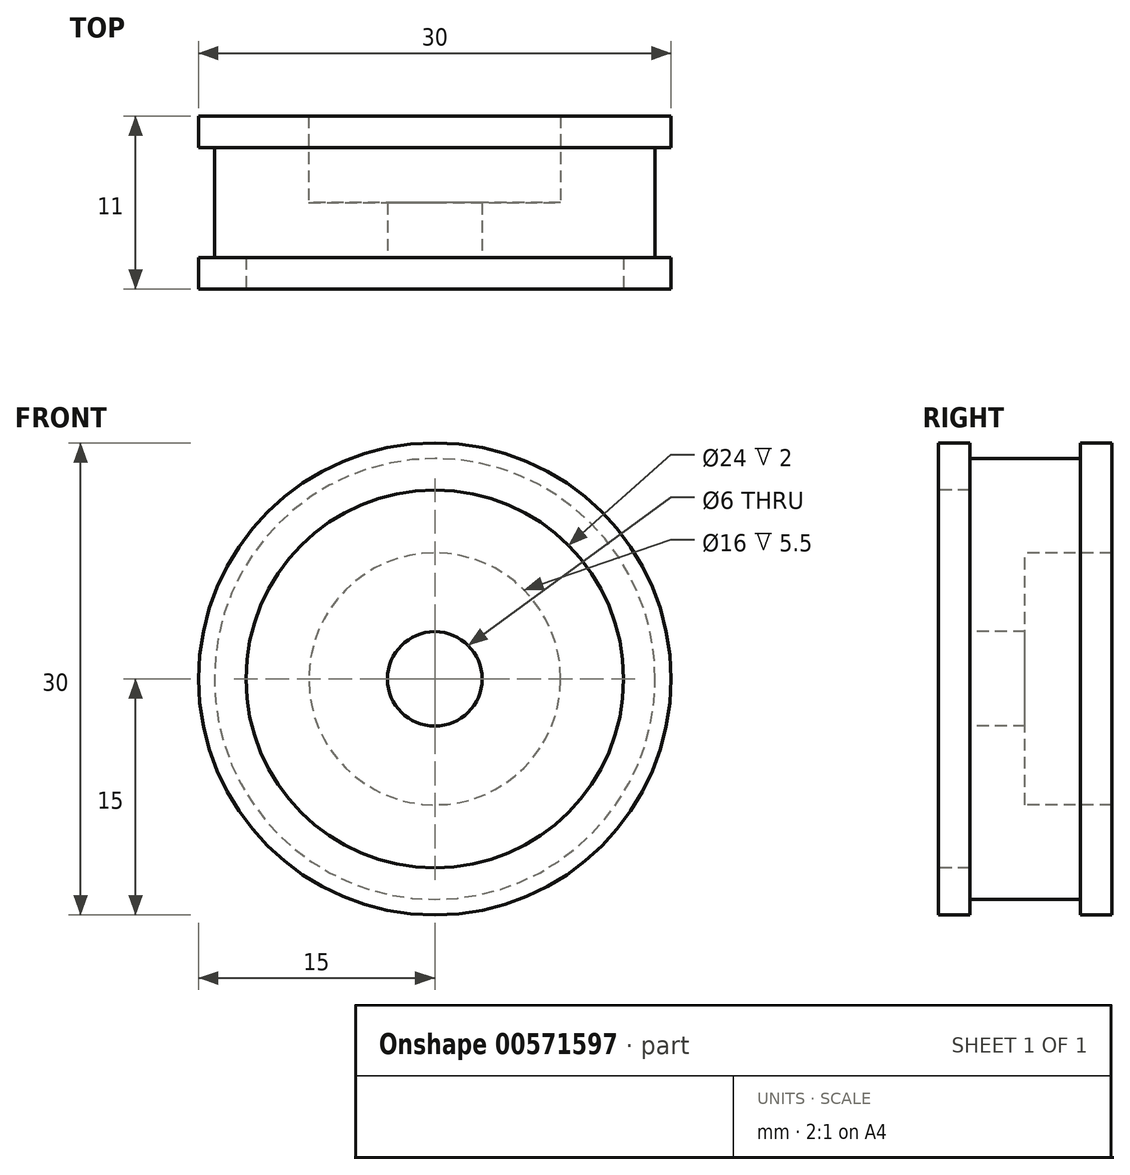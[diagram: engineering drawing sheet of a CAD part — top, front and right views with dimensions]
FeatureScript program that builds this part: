
annotation { "Feature Type Name" : "Feature", "Feature Type Description" : "" }
export const myFeature = defineFeature(function(context is Context, id is Id, definition is map)
    precondition{}
    {
        {
            var Q0;
            Q0=qCreatedBy(makeId("Top.planeOp"),FACE);
            var sketch = newSketch(context, id + "F0", { "sketchPlane" : qUnion([Q0])});
            skLineSegment(sketch, "E0", {"start": v(-15, 13.14) * mm, "end": v(-15, 11.14) * mm});
            skLineSegment(sketch, "E1", {"start": v(-15, 11.14) * mm, "end": v(-14, 11.14) * mm});
            skLineSegment(sketch, "E2", {"start": v(-14, 11.14) * mm, "end": v(-14, 4.14) * mm});
            skLineSegment(sketch, "E3", {"start": v(-14, 4.14) * mm, "end": v(-15, 4.14) * mm});
            skLineSegment(sketch, "E4", {"start": v(-15, 4.14) * mm, "end": v(-15, 2.14) * mm});
            skLineSegment(sketch, "E5", {"start": v(-12, 2.14) * mm, "end": v(-12, 4.14) * mm});
            skLineSegment(sketch, "E6", {"start": v(-12, 4.14) * mm, "end": v(-3, 4.14) * mm});
            skLineSegment(sketch, "E7", {"start": v(-3, 4.14) * mm, "end": v(-3, 7.64) * mm});
            skLineSegment(sketch, "E8", {"start": v(-3, 7.64) * mm, "end": v(-8, 7.64) * mm});
            skLineSegment(sketch, "E9", {"start": v(-8, 7.64) * mm, "end": v(-8, 13.14) * mm});
            skLineSegment(sketch, "E10", {"start": v(-15, 13.14) * mm, "end": v(-8, 13.14) * mm});
            skLineSegment(sketch, "E11", {"start": v(-15, 2.14) * mm, "end": v(-12, 2.14) * mm});
            skLineSegment(sketch, "E12", {"start": v(0, 1.71) * mm, "end": v(0, 7.64) * mm, "construction": true});
            skSolve(sketch);
        }
        {
            var Q0;
            Q0=makeQuery(id+"F0.imprint","IMPRINT",FACE,{"disambiguationData":[TD([[makeQuery(id+"F0.imprint","IMPRINT",EDGE,{"derivedFrom":sQuery(id+"F0.wireOp",EDGE,"E0")}),1.0]])]});
            var Q1;
            Q1=sQuery(id+"F0.wireOp",EDGE,"E12");
            revolve(context, id + "F1", {"entities" : qUnion([Q0]), "axis" : qUnion([Q1]), "revolveType" : RevolveType.FULL});
        }
    });
